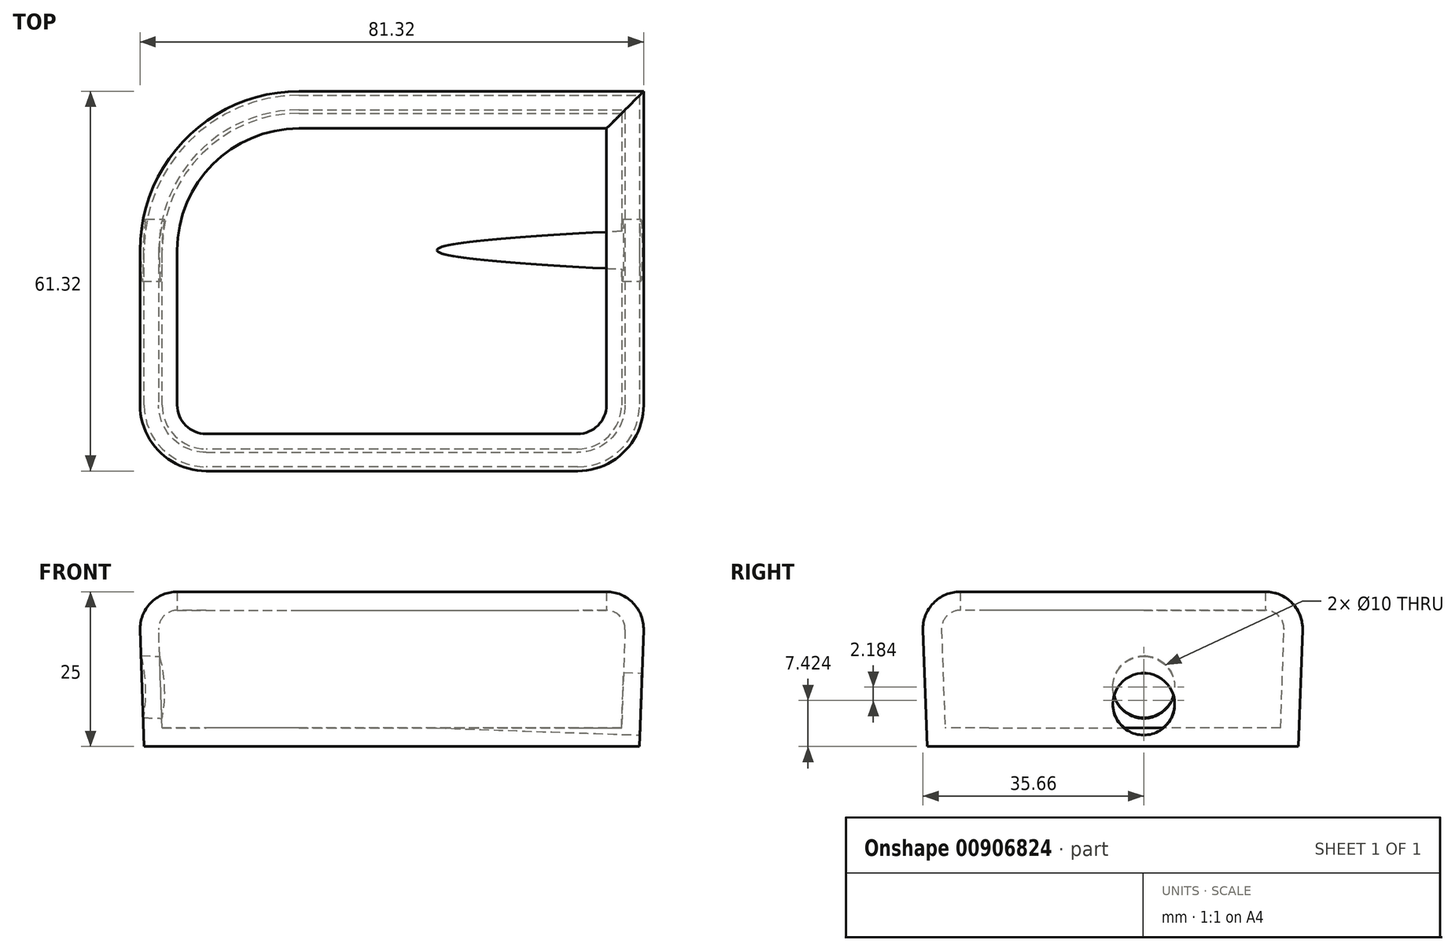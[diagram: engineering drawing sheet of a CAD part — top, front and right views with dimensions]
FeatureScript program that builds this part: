
annotation { "Feature Type Name" : "Feature", "Feature Type Description" : "" }
export const myFeature = defineFeature(function(context is Context, id is Id, definition is map)
    precondition{}
    {
        {
            var Q0;
            Q0=qCreatedBy(makeId("Top.planeOp"),FACE);
            var sketch = newSketch(context, id + "F0", { "sketchPlane" : qUnion([Q0])});
            skLineSegment(sketch, "E0.bottom", {"start": v(0, 25) * mm, "end": v(55, 25) * mm});
            skLineSegment(sketch, "E0.top", {"start": v(-15, -35) * mm, "end": v(45, -35) * mm});
            skLineSegment(sketch, "E0.left", {"start": v(-25, 0) * mm, "end": v(-25, -25) * mm});
            skLineSegment(sketch, "E0.right", {"start": v(55, 25) * mm, "end": v(55, -25) * mm});
            skArc(sketch, "E1", {"start": v(0, 25) * mm, "mid": v(-17.68, 17.68) * mm, "end": v(-25, 0) * mm});
            skPoint(sketch, "E2.visualSharp", {"position": v(-25, -35) * mm});
            skArc(sketch, "E2.filletArc", {"start": v(-25, -25) * mm, "mid": v(-22.07, -32.07) * mm, "end": v(-15, -35) * mm});
            skPoint(sketch, "E3.visualSharp", {"position": v(55, -35) * mm});
            skArc(sketch, "E3.filletArc", {"start": v(45, -35) * mm, "mid": v(52.07, -32.07) * mm, "end": v(55, -25) * mm});
            skSolve(sketch);
        }
        {
            var Q0;
            Q0=makeQuery(id+"F0.imprint","IMPRINT",FACE,{"disambiguationData":[TD([[makeQuery(id+"F0.imprint","IMPRINT",EDGE,{"derivedFrom":sQuery(id+"F0.wireOp",EDGE,"E0.bottom")}),-1.0]])]});
            extrude(context, id + "F1", {"entities" : qUnion([Q0]), "depth" : 25 * mm, "offsetDistance" : 25 * mm, "hasDraft" : true, "draftAngle" : 2 * degree});
        }
        {
            var Q0;
            Q0=makeQuery(id+"F1.opExtrude","CAP_EDGE",EDGE,{"disambiguationData":[OSD([sQuery(id+"F0.wireOp",EDGE,"E0.top")])],"isStart":false});
            fillet(context, id + "F2", {"entities" : qUnion([Q0]), "radius" : 6 * mm, "tangentPropagation" : true, "allowEdgeOverflow" : false});
        }
        {
            var Q0;
            Q0=makeQuery(id+"F1.opExtrude","CAP_FACE",FACE,{"disambiguationData":[OSD([sQuery(id+"F0.wireOp",EDGE,"E0.bottom"),sQuery(id+"F0.wireOp",EDGE,"E0.top"),sQuery(id+"F0.wireOp",EDGE,"E0.left"),sQuery(id+"F0.wireOp",EDGE,"E0.right"),sQuery(id+"F0.wireOp",EDGE,"E1"),sQuery(id+"F0.wireOp",EDGE,"E2.filletArc"),sQuery(id+"F0.wireOp",EDGE,"E3.filletArc")])],"isStart":false});
            shell(context, id + "F3", {"entities" : qUnion([Q0]), "thickness" : 3 * mm});
        }
        {
            var Q0;
            Q0=makeQuery(id+"F1.opExtrude","SWEPT_FACE",FACE,{"disambiguationData":[OSD([sQuery(id+"F0.wireOp",EDGE,"E0.right")])]});
            var sketch = newSketch(context, id + "F4", { "sketchPlane" : qUnion([Q0])});
            skCircle(sketch, "E4", {"center": v(0, 8.78) * mm, "radius": 5.36 * mm});
            skSolve(sketch);
        }
        {
            var Q0;
            Q0=sQuery(id+"F4.wireOp",VERTEX,"E4.center");
            var Q1;
            Q1=makeQuery(id+"F1.opExtrude","SWEPT_BODY",BODY,{"disambiguationData":[OSD([sQuery(id+"F0.wireOp",EDGE,"E0.bottom"),sQuery(id+"F0.wireOp",EDGE,"E0.top"),sQuery(id+"F0.wireOp",EDGE,"E0.left"),sQuery(id+"F0.wireOp",EDGE,"E0.right"),sQuery(id+"F0.wireOp",EDGE,"E1"),sQuery(id+"F0.wireOp",EDGE,"E2.filletArc"),sQuery(id+"F0.wireOp",EDGE,"E3.filletArc")])]});
            hole(context, id + "F5", {"style" : HoleStyle.SIMPLE, "endStyle" : HoleEndStyle.THROUGH, "holeDiameter" : 10 * mm, "majorDiameter" : 5 * mm, "isTappedThrough" : true, "tappedDepth" : 12 * mm, "tapClearance" : 3, "locations" : qUnion([Q0]), "scope" : qUnion([Q1])});
        }
    });
